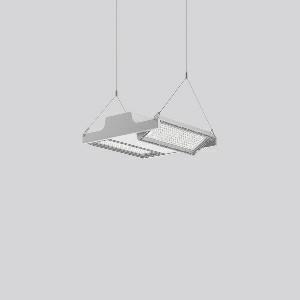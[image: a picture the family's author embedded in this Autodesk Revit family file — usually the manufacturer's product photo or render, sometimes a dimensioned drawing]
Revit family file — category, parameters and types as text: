
# Revit family: light_case_921682_004_76_6553
name_source: partatom
category: Lighting Fixtures
units: mm (PartAtom-declared; Revit-internal decimal feet)

## family parameters
Cut with Voids When Loaded = No
Host = Face
Light Source = No
Part Type = Normal
Room Calculation Point = No
Round Connector Dimension = Use Diameter
Shared = No

## types (1)
- LIGHT CASE (1 x LED Modul 840, 8900 lm, 4000)
    Apparent Load = 117 VA
    CIE Flux Codes = 81 98 100 100 100
    Color Rendering = 80
    Color Temperature = 4000
    Default Elevation = 1800 mm
    Description = Series: LIGHT CASE
Flat highbay luminaire for chain or cable suspension with 2 LED modules that can be swivelled. Housing: die cast aluminium and sheet steel, powder-coated. Optimised thermal management thanks to special luminaire design. Self-cleaning heat sink for constant heat dissipation. Cover: plastic (polycarbonate, shockproof), with integrated four-row lens system. LED modules can be swivelled ± 30° for optimum illumination. Suitable for chain or steel cable suspension (to be provided on site). With 5-pin connection terminal (1.5 m). With integrated movement sensor and light sensor for daylight detection on request. Ball impact proof in accordance with DIN 18032-03 (except steel cable suspension). Luminaire with limited surface temperature in accordance with EN 60598-2-24 for use in environments in which a deposit of conductive dust on the luminaire can be expected. 
Colour: silver, matt (approx. RAL 9006)
Length: 406 mm
Width: 397 mm
Height: 110 mm
Lamp: LED
Socket: without socket
Colour temperature: 4000K
Colour rendering index (CRI): 80
System power: 117 W
Rated luminous flux: 17800 lm
Luminous efficiency: 152 lm/W
Control gear: Converter, dimmable, DALI
Protection class: I
Type of protection: IP 65
    Height = 110 mm
    Lamp = 1 x LED Modul 840
    Lamp Light Flux = 8900 lm
    Lamp count = 1
    Length = 406 mm
    Lifetime = 50000 h
    Luminous efficacy = 152 lm/W
    Manufacturer = RZB
    ModVariant = No
    Model = 921682.004.76
    Mounting Place = Ceiling
    Mounting Type = Pendant
    Number of Poles = 1
    OnlyDefault = Yes
    Power Factor = 1
    Product Name = LIGHT CASE
    Product group = Pendant commercial luminaires
    ProductGroupID = 903
    Protection Class = Protection class I
    Protection Degree = IP 65
    RLX_Detail_Level = 1
    RLX_Emergency_Light_Flux = 0 lm
    RLX_Emergency_Type = 0
    RLX_Emergency_Type_DB = No
    RlxData = <blob elided: 25041 chars, md5=0006fddd>
    Socket = socket
    Standby Power = 0 W
    System Light Flux = 17800 lm
    System Power = 117 W
    Type Comments = Product without accessories
    Type Image = 921517.004.76.jpg
    URL = http://relux.com
    VarID = ---
    Voltage = 230 V
    Voltage Range = 220-240 V
    Weight = 0.00 kg
    Width = 397 mm

## geometry (parser evidence)
native form markers: Blend x4, Sweep x16
no freeform markers — native parametric forms only
